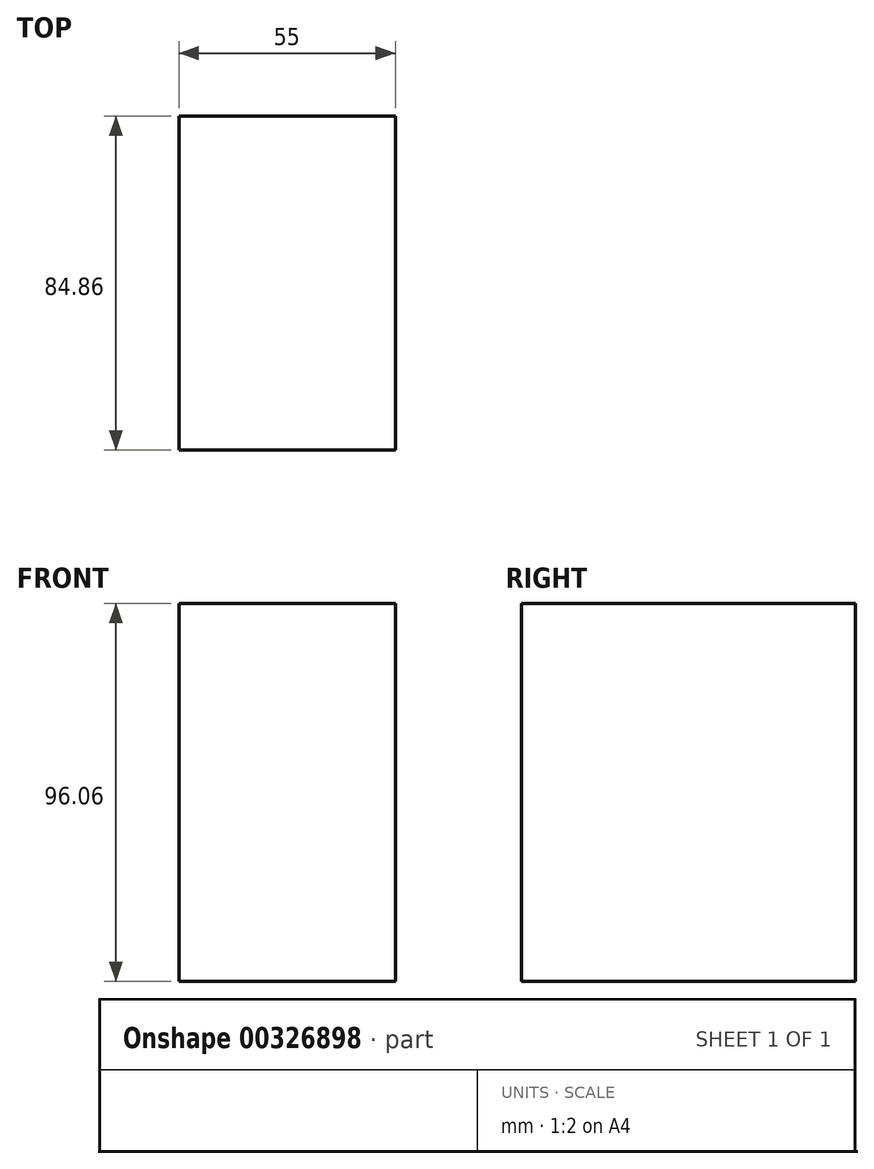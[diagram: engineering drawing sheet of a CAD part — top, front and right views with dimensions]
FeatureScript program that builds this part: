
annotation { "Feature Type Name" : "Feature", "Feature Type Description" : "" }
export const myFeature = defineFeature(function(context is Context, id is Id, definition is map)
    precondition{}
    {
        {
            var Q0;
            Q0=qCreatedBy(makeId("Right.planeOp"),FACE);
            var sketch = newSketch(context, id + "F0", { "sketchPlane" : qUnion([Q0])});
            skLineSegment(sketch, "E0.bottom", {"start": v(-42.43, 48.03) * mm, "end": v(42.43, 48.03) * mm});
            skLineSegment(sketch, "E0.top", {"start": v(-42.43, -48.03) * mm, "end": v(42.43, -48.03) * mm});
            skLineSegment(sketch, "E0.left", {"start": v(-42.43, 48.03) * mm, "end": v(-42.43, -48.03) * mm});
            skLineSegment(sketch, "E0.right", {"start": v(42.43, 48.03) * mm, "end": v(42.43, -48.03) * mm});
            skPoint(sketch, "E0.middle", {"position": v(0, 0) * mm});
            skSolve(sketch);
        }
        {
            var Q0;
            Q0 = qSketchRegion(id + "F0", true);
            extrude(context, id + "F1", {"entities" : qUnion([Q0]), "depth" : 55 * mm});
        }
    });
